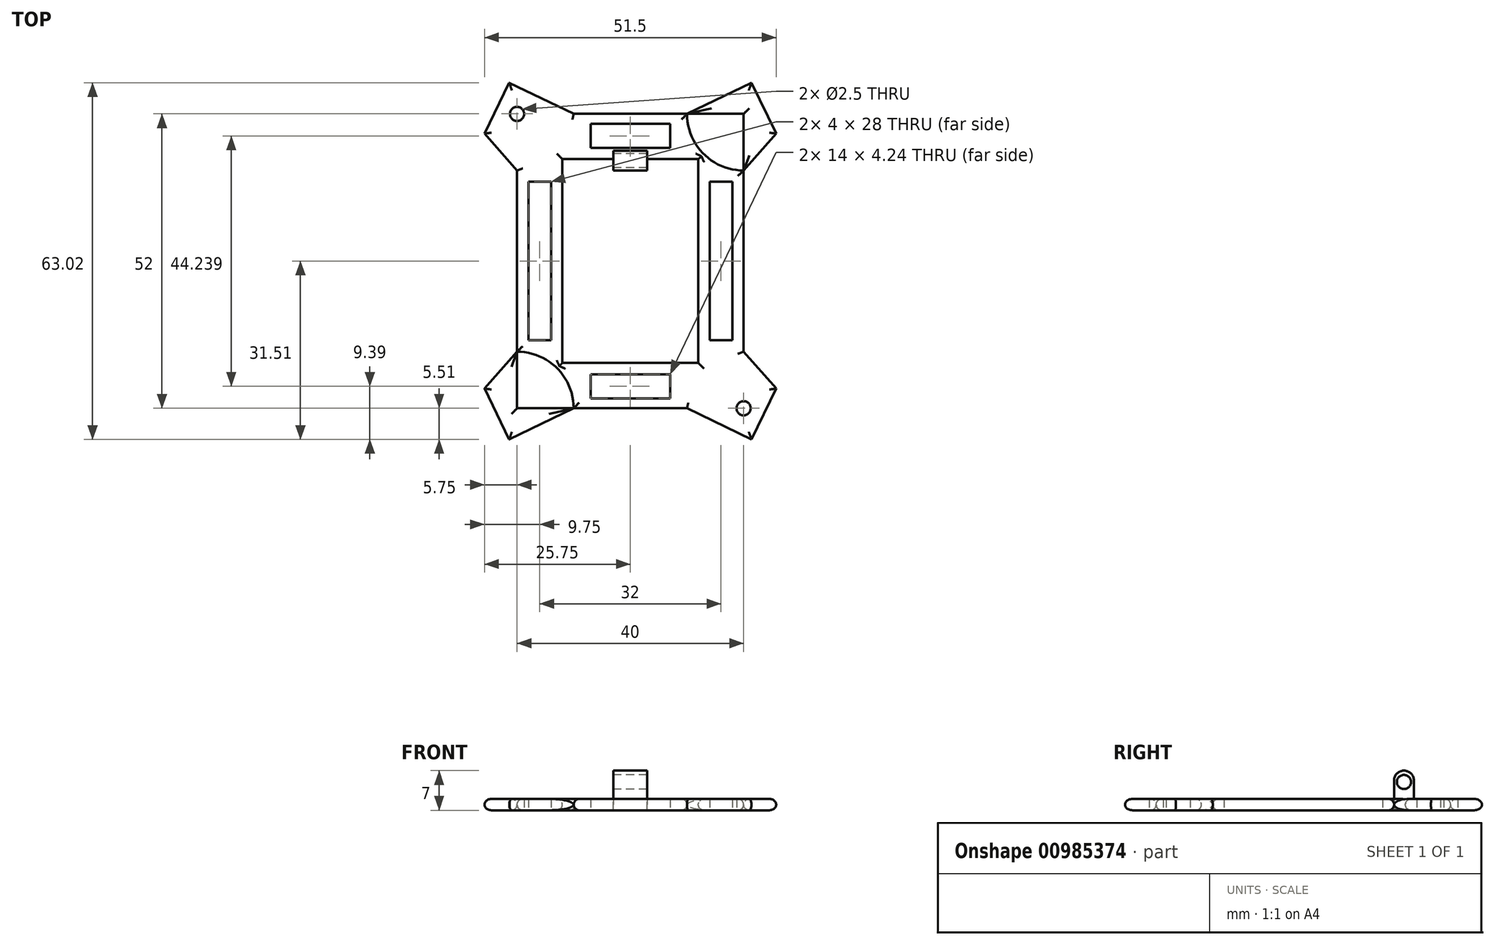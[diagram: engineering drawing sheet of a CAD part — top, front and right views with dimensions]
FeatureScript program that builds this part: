
annotation { "Feature Type Name" : "Feature", "Feature Type Description" : "" }
export const myFeature = defineFeature(function(context is Context, id is Id, definition is map)
    precondition{}
    {
        {
            var Q0;
            Q0=qCreatedBy(makeId("Top.planeOp"),FACE);
            var sketch = newSketch(context, id + "F0", { "sketchPlane" : qUnion([Q0])});
            skPoint(sketch, "E0.middle", {"position": v(0, 0) * mm});
            skLineSegment(sketch, "E1.bottom", {"start": v(10, -16) * mm, "end": v(-10, -16) * mm});
            skLineSegment(sketch, "E1.top", {"start": v(10, 16) * mm, "end": v(-10, 16) * mm});
            skLineSegment(sketch, "E1.left", {"start": v(10, -16) * mm, "end": v(10, 16) * mm});
            skLineSegment(sketch, "E1.right", {"start": v(-10, -16) * mm, "end": v(-10, 16) * mm});
            skLineSegment(sketch, "E2.bottom", {"start": v(12, 18) * mm, "end": v(-12, 18) * mm});
            skLineSegment(sketch, "E2.top", {"start": v(12, -18) * mm, "end": v(-12, -18) * mm});
            skLineSegment(sketch, "E2.left", {"start": v(12, 18) * mm, "end": v(12, -18) * mm});
            skLineSegment(sketch, "E2.right", {"start": v(-12, 18) * mm, "end": v(-12, -18) * mm});
            skLineSegment(sketch, "E3.bottom", {"start": v(20, -26) * mm, "end": v(-20, -26) * mm});
            skLineSegment(sketch, "E3.top", {"start": v(20, 26) * mm, "end": v(-20, 26) * mm});
            skLineSegment(sketch, "E3.left", {"start": v(20, -26) * mm, "end": v(20, 26) * mm});
            skLineSegment(sketch, "E3.right", {"start": v(-20, -26) * mm, "end": v(-20, 26) * mm});
            skCircle(sketch, "E4", {"center": v(-20, 26) * mm, "radius": 10 * mm});
            skCircle(sketch, "E5", {"center": v(20, 26) * mm, "radius": 10 * mm});
            skCircle(sketch, "E6", {"center": v(20, -26) * mm, "radius": 10 * mm});
            skCircle(sketch, "E7", {"center": v(-20, -26) * mm, "radius": 10 * mm});
            skCircle(sketch, "E8", {"center": v(-20, 26) * mm, "radius": 1.25 * mm});
            skCircle(sketch, "E9.MirrorC", {"center": v(20, 26) * mm, "radius": 1.25 * mm});
            skCircle(sketch, "E10.MirrorC", {"center": v(-20, -26) * mm, "radius": 1.25 * mm});
            skCircle(sketch, "E11.MirrorC", {"center": v(20, -26) * mm, "radius": 1.25 * mm});
            skLineSegment(sketch, "E12", {"start": v(-3, 16) * mm, "end": v(-3, 18) * mm});
            skLineSegment(sketch, "E13", {"start": v(3, 16) * mm, "end": v(3, 18) * mm});
            skLineSegment(sketch, "E14.bottom", {"start": v(-3, 18) * mm, "end": v(3, 18) * mm});
            skLineSegment(sketch, "E14.top", {"start": v(-3, 19.5) * mm, "end": v(3, 19.5) * mm});
            skLineSegment(sketch, "E14.left", {"start": v(-3, 18) * mm, "end": v(-3, 19.5) * mm});
            skLineSegment(sketch, "E14.right", {"start": v(3, 18) * mm, "end": v(3, 19.5) * mm});
            skLineSegment(sketch, "E15", {"start": v(-10, 26) * mm, "end": v(-26.2, 33.85) * mm});
            skLineSegment(sketch, "E16", {"start": v(-29.92, 27.25) * mm, "end": v(-20, 16) * mm});
            skLineSegment(sketch, "E17.MirrorCS", {"start": v(10, 26) * mm, "end": v(26.2, 33.85) * mm});
            skLineSegment(sketch, "E18.MirrorCS", {"start": v(29.92, 27.25) * mm, "end": v(20, 16) * mm});
            skLineSegment(sketch, "E19.MirrorCS", {"start": v(29.92, -27.25) * mm, "end": v(20, -16) * mm});
            skLineSegment(sketch, "E20.MirrorCS", {"start": v(10, -26) * mm, "end": v(26.2, -33.85) * mm});
            skLineSegment(sketch, "E21.MirrorCS", {"start": v(-10, -26) * mm, "end": v(-26.2, -33.85) * mm});
            skLineSegment(sketch, "E22.MirrorCS", {"start": v(-29.92, -27.25) * mm, "end": v(-20, -16) * mm});
            skLineSegment(sketch, "E23", {"start": v(-10, 16) * mm, "end": v(-10, 18) * mm});
            skLineSegment(sketch, "E24", {"start": v(10, 16) * mm, "end": v(10, 18) * mm});
            skLineSegment(sketch, "E25", {"start": v(-21.39, 31.51) * mm, "end": v(-25.75, 22.51) * mm});
            skLineSegment(sketch, "E26.MirrorCS", {"start": v(21.39, 31.51) * mm, "end": v(25.75, 22.51) * mm});
            skLineSegment(sketch, "E27.MirrorCS", {"start": v(-21.39, -31.51) * mm, "end": v(-25.75, -22.51) * mm});
            skLineSegment(sketch, "E28.MirrorCS", {"start": v(21.39, -31.51) * mm, "end": v(25.75, -22.51) * mm});
            skLineSegment(sketch, "E29.bottom", {"start": v(-18, 14) * mm, "end": v(-14, 14) * mm});
            skLineSegment(sketch, "E29.top", {"start": v(-18, -14) * mm, "end": v(-14, -14) * mm});
            skLineSegment(sketch, "E29.left", {"start": v(-18, 14) * mm, "end": v(-18, -14) * mm});
            skLineSegment(sketch, "E29.right", {"start": v(-14, 14) * mm, "end": v(-14, -14) * mm});
            skLineSegment(sketch, "E30.MirrorCS", {"start": v(14, 14) * mm, "end": v(14, -14) * mm});
            skLineSegment(sketch, "E31.MirrorCS", {"start": v(18, 14) * mm, "end": v(14, 14) * mm});
            skLineSegment(sketch, "E32.MirrorCS", {"start": v(18, 14) * mm, "end": v(18, -14) * mm});
            skLineSegment(sketch, "E33.MirrorCS", {"start": v(18, -14) * mm, "end": v(14, -14) * mm});
            skLineSegment(sketch, "E34.bottom", {"start": v(-7, -20) * mm, "end": v(7, -20) * mm});
            skLineSegment(sketch, "E34.top", {"start": v(-7, -24.24) * mm, "end": v(7, -24.24) * mm});
            skLineSegment(sketch, "E34.left", {"start": v(-7, -20) * mm, "end": v(-7, -24.24) * mm});
            skLineSegment(sketch, "E34.right", {"start": v(7, -20) * mm, "end": v(7, -24.24) * mm});
            skLineSegment(sketch, "E35.MirrorCS", {"start": v(-7, 20) * mm, "end": v(7, 20) * mm});
            skLineSegment(sketch, "E36.MirrorCS", {"start": v(-7, 20) * mm, "end": v(-7, 24.24) * mm});
            skLineSegment(sketch, "E37.MirrorCS", {"start": v(-7, 24.24) * mm, "end": v(7, 24.24) * mm});
            skLineSegment(sketch, "E38.MirrorCS", {"start": v(7, 20) * mm, "end": v(7, 24.24) * mm});
            skSolve(sketch);
        }
        {
            var Q0;
            {var subQ0=sQuery(id+"F0.wireOp",EDGE,"XfmaCdGe-Nsh5-LR8N-U050-nXJdRo87k7nu");Q0=makeQuery(id+"F0.imprint","IMPRINT",FACE,{"disambiguationData":[TD([[makeQuery(id+"F0.imprint","IMPRINT",EDGE,{"derivedFrom":subQ0}),-1.0]])]});}
            var Q1;
            {var subQ0=sQuery(id+"F0.wireOp",EDGE,"67c493aa-9df7-43f4-b791-e47cdcb916b60.MirrorCS");Q1=makeQuery(id+"F0.imprint","IMPRINT",FACE,{"disambiguationData":[TD([[makeQuery(id+"F0.imprint","IMPRINT",EDGE,{"derivedFrom":subQ0}),-1.0]])]});}
            var Q2;
            {var subQ0=sQuery(id+"F0.wireOp",EDGE,"3c266ea2-0ddf-4ded-b89f-077357a7d8e80.MirrorCS");Q2=makeQuery(id+"F0.imprint","IMPRINT",FACE,{"disambiguationData":[TD([[makeQuery(id+"F0.imprint","IMPRINT",EDGE,{"derivedFrom":subQ0}),-1.0]])]});}
            var Q3;
            {var subQ0=sQuery(id+"F0.wireOp",EDGE,"ab4d64e5-a29a-4c87-9f54-f3676ced8fba0.MirrorCS");Q3=makeQuery(id+"F0.imprint","IMPRINT",FACE,{"disambiguationData":[TD([[makeQuery(id+"F0.imprint","IMPRINT",EDGE,{"derivedFrom":subQ0}),1.0]])]});}
            var Q4;
            Q4=makeQuery(id+"F0.imprint","IMPRINT",FACE,{"disambiguationData":[TD([[makeQuery(id+"F0.imprint","IMPRINT",EDGE,{"derivedFrom":sQuery(id+"F0.wireOp",EDGE,"oP3ZfhLO-5z78-oQSo-uuvH-yzJxo6IJEnQO")}),-1.0]])]});
            var Q5;
            Q5=makeQuery(id+"F0.imprint","IMPRINT",FACE,{"disambiguationData":[TD([[makeQuery(id+"F0.imprint","IMPRINT",EDGE,{"derivedFrom":sQuery(id+"F0.wireOp",EDGE,"5d5cfb4f-1e90-434a-910e-95713f9e32be0.MirrorC")}),1.0]])]});
            var Q6;
            Q6=makeQuery(id+"F0.imprint","IMPRINT",FACE,{"disambiguationData":[TD([[makeQuery(id+"F0.imprint","IMPRINT",EDGE,{"derivedFrom":sQuery(id+"F0.wireOp",EDGE,"24c43ebd-9ed0-4dd5-8c82-3635907a6bdc0.MirrorC")}),-1.0]])]});
            var Q7;
            Q7=makeQuery(id+"F0.imprint","IMPRINT",FACE,{"disambiguationData":[TD([[makeQuery(id+"F0.imprint","IMPRINT",EDGE,{"derivedFrom":sQuery(id+"F0.wireOp",EDGE,"ed7e95fd-fa47-4424-be7c-35b6ced3335c0.MirrorC")}),1.0]])]});
            var Q8;
            Q8=makeQuery(id+"F0.imprint","IMPRINT",FACE,{"disambiguationData":[TD([[makeQuery(id+"F0.imprint","IMPRINT",EDGE,{"derivedFrom":sQuery(id+"F0.wireOp",EDGE,"E2.top")}),1.0]])]});
            var Q9;
            {var subQ1=sQuery(id+"F0.wireOp",EDGE,"E3.top");var subQ3=sQuery(id+"F0.wireOp",EDGE,"E8");var subQ4=makeQuery(id+"F0.imprint","INTERSECT",VERTEX,{"derivedFrom":[subQ1,subQ3]});Q9=makeQuery(id+"F0.imprint","IMPRINT",FACE,{"disambiguationData":[TD([[makeQuery(id+"F0.imprint","IMPRINT",EDGE,{"disambiguationData":[TD([[subQ4,1.0]])],"derivedFrom":subQ3}),-1.0]])]});}
            var Q10;
            {var subQ4=sQuery(id+"F0.wireOp",EDGE,"E25");Q10=makeQuery(id+"F0.imprint","IMPRINT",FACE,{"disambiguationData":[TD([[makeQuery(id+"F0.imprint","IMPRINT",EDGE,{"derivedFrom":subQ4}),1.0]])]});}
            var Q11;
            {var subQ1=sQuery(id+"F0.wireOp",EDGE,"E3.top");var subQ3=sQuery(id+"F0.wireOp",EDGE,"E9.MirrorC");var subQ4=makeQuery(id+"F0.imprint","INTERSECT",VERTEX,{"derivedFrom":[subQ1,subQ3]});Q11=makeQuery(id+"F0.imprint","IMPRINT",FACE,{"disambiguationData":[TD([[makeQuery(id+"F0.imprint","IMPRINT",EDGE,{"disambiguationData":[TD([[subQ4,1.0]])],"derivedFrom":subQ3}),1.0]])]});}
            var Q12;
            {var subQ4=sQuery(id+"F0.wireOp",EDGE,"E26.MirrorCS");Q12=makeQuery(id+"F0.imprint","IMPRINT",FACE,{"disambiguationData":[TD([[makeQuery(id+"F0.imprint","IMPRINT",EDGE,{"derivedFrom":subQ4}),-1.0]])]});}
            var Q13;
            {var subQ1=sQuery(id+"F0.wireOp",EDGE,"E3.bottom");var subQ3=sQuery(id+"F0.wireOp",EDGE,"E11.MirrorC");var subQ4=makeQuery(id+"F0.imprint","INTERSECT",VERTEX,{"derivedFrom":[subQ1,subQ3]});Q13=makeQuery(id+"F0.imprint","IMPRINT",FACE,{"disambiguationData":[TD([[makeQuery(id+"F0.imprint","IMPRINT",EDGE,{"disambiguationData":[TD([[subQ4,1.0]])],"derivedFrom":subQ3}),-1.0]])]});}
            var Q14;
            {var subQ8=sQuery(id+"F0.wireOp",EDGE,"E28.MirrorCS");Q14=makeQuery(id+"F0.imprint","IMPRINT",FACE,{"disambiguationData":[TD([[makeQuery(id+"F0.imprint","IMPRINT",EDGE,{"derivedFrom":subQ8}),1.0]])]});}
            var Q15;
            {var subQ8=sQuery(id+"F0.wireOp",EDGE,"E27.MirrorCS");Q15=makeQuery(id+"F0.imprint","IMPRINT",FACE,{"disambiguationData":[TD([[makeQuery(id+"F0.imprint","IMPRINT",EDGE,{"derivedFrom":subQ8}),-1.0]])]});}
            var Q16;
            {var subQ1=sQuery(id+"F0.wireOp",EDGE,"E3.bottom");var subQ3=sQuery(id+"F0.wireOp",EDGE,"E10.MirrorC");var subQ4=makeQuery(id+"F0.imprint","INTERSECT",VERTEX,{"derivedFrom":[subQ1,subQ3]});Q16=makeQuery(id+"F0.imprint","IMPRINT",FACE,{"disambiguationData":[TD([[makeQuery(id+"F0.imprint","IMPRINT",EDGE,{"disambiguationData":[TD([[subQ4,1.0]])],"derivedFrom":subQ3}),1.0]])]});}
            extrude(context, id + "F1", {"entities" : qUnion([Q0, Q1, Q2, Q3, Q4, Q5, Q6, Q7, Q8, Q9, Q10, Q11, Q12, Q13, Q14, Q15, Q16]), "depth" : 2 * mm, "offsetDistance" : 25 * mm});
        }
        {
            var Q0;
            {var subQ0=sQuery(id+"F0.wireOp",EDGE,"E12");Q0=makeQuery(id+"F0.imprint","IMPRINT",FACE,{"disambiguationData":[TD([[makeQuery(id+"F0.imprint","IMPRINT",EDGE,{"derivedFrom":subQ0}),-1.0]])]});}
            var Q1;
            Q1=makeQuery(id+"F0.imprint","IMPRINT",FACE,{"disambiguationData":[TD([[makeQuery(id+"F0.imprint","IMPRINT",EDGE,{"derivedFrom":sQuery(id+"F0.wireOp",EDGE,"E14.top")}),-1.0]])]});
            extrude(context, id + "F2", {"entities" : qUnion([Q0, Q1]), "operationType" : NewBodyOperationType.ADD, "depth" : 7 * mm, "offsetDistance" : 25 * mm});
        }
        {
            var Q0;
            Q0=makeQuery(id+"F2.opExtrude","CAP_EDGE",EDGE,{"disambiguationData":[OSD([sQuery(id+"F0.wireOp",EDGE,"E1.top")])],"isStart":false});
            var Q1;
            Q1=makeQuery(id+"F2.opExtrude","CAP_EDGE",EDGE,{"disambiguationData":[OSD([sQuery(id+"F0.wireOp",EDGE,"E2.bottom")])],"isStart":false});
            var Q2;
            Q2=makeQuery(id+"F2.opExtrude","CAP_EDGE",EDGE,{"disambiguationData":[OSD([sQuery(id+"F0.wireOp",EDGE,"E14.top")])],"isStart":false});
            fillet(context, id + "F3", {"entities" : qUnion([Q0, Q1, Q2]), "radius" : 1.75 * mm, "tangentPropagation" : true, "allowEdgeOverflow" : false});
        }
        {
            var Q0;
            Q0=makeQuery(id+"F2.opExtrude","SWEPT_FACE",FACE,{"disambiguationData":[OSD([sQuery(id+"F0.wireOp",EDGE,"E12"),sQuery(id+"F0.wireOp",EDGE,"E14.left")])]});
            var sketch = newSketch(context, id + "F4", { "sketchPlane" : qUnion([Q0])});
            skCircle(sketch, "E39", {"center": v(-17.75, 5) * mm, "radius": 1.25 * mm});
            skPoint(sketch, "E39.centerSnap0", {"position": v(-17.75, 7) * mm});
            skSolve(sketch);
        }
        {
            var Q0;
            Q0=makeQuery(id+"F4.imprint","IMPRINT",FACE,{"disambiguationData":[TD([[makeQuery(id+"F4.imprint","IMPRINT",EDGE,{"derivedFrom":sQuery(id+"F4.wireOp",EDGE,"E39")}),1.0]])]});
            extrude(context, id + "F5", {"entities" : qUnion([Q0]), "operationType" : NewBodyOperationType.REMOVE, "oppositeDirection" : true, "depth" : 25 * mm, "offsetDistance" : 25 * mm});
        }
        {
            var Q0;
            Q0=makeQuery(id+"F1.opExtrude","CAP_EDGE",EDGE,{"disambiguationData":[OSD([sQuery(id+"F0.wireOp",EDGE,"E3.right")])],"isStart":false});
            var Q1;
            Q1=makeQuery(id+"F1.opExtrude","CAP_EDGE",EDGE,{"disambiguationData":[OSD([sQuery(id+"F0.wireOp",EDGE,"E7")])],"isStart":false});
            var Q2;
            Q2=makeQuery(id+"F1.opExtrude","CAP_EDGE",EDGE,{"disambiguationData":[OSD([sQuery(id+"F0.wireOp",EDGE,"E3.bottom")])],"isStart":false});
            var Q3;
            Q3=makeQuery(id+"F1.opExtrude","CAP_EDGE",EDGE,{"disambiguationData":[OSD([sQuery(id+"F0.wireOp",EDGE,"E6")])],"isStart":false});
            var Q4;
            Q4=makeQuery(id+"F1.opExtrude","CAP_EDGE",EDGE,{"disambiguationData":[OSD([sQuery(id+"F0.wireOp",EDGE,"E3.left")])],"isStart":false});
            var Q5;
            Q5=makeQuery(id+"F1.opExtrude","CAP_EDGE",EDGE,{"disambiguationData":[OSD([sQuery(id+"F0.wireOp",EDGE,"E5")])],"isStart":false});
            var Q6;
            Q6=makeQuery(id+"F1.opExtrude","CAP_EDGE",EDGE,{"disambiguationData":[OSD([sQuery(id+"F0.wireOp",EDGE,"E3.top")])],"isStart":false});
            var Q7;
            Q7=makeQuery(id+"F1.opExtrude","CAP_EDGE",EDGE,{"disambiguationData":[OSD([sQuery(id+"F0.wireOp",EDGE,"E4")])],"isStart":false});
            var Q8;
            Q8=makeQuery(id+"F1.opExtrude","CAP_EDGE",EDGE,{"disambiguationData":[OSD([sQuery(id+"F0.wireOp",EDGE,"E4")])],"isStart":true});
            var Q9;
            Q9=makeQuery(id+"F1.opExtrude","CAP_EDGE",EDGE,{"disambiguationData":[OSD([sQuery(id+"F0.wireOp",EDGE,"E3.top")])],"isStart":true});
            var Q10;
            Q10=makeQuery(id+"F1.opExtrude","CAP_EDGE",EDGE,{"disambiguationData":[OSD([sQuery(id+"F0.wireOp",EDGE,"E5")])],"isStart":true});
            var Q11;
            Q11=makeQuery(id+"F1.opExtrude","CAP_EDGE",EDGE,{"disambiguationData":[OSD([sQuery(id+"F0.wireOp",EDGE,"E3.left")])],"isStart":true});
            var Q12;
            Q12=makeQuery(id+"F1.opExtrude","CAP_EDGE",EDGE,{"disambiguationData":[OSD([sQuery(id+"F0.wireOp",EDGE,"E7")])],"isStart":true});
            var Q13;
            Q13=makeQuery(id+"F1.opExtrude","CAP_EDGE",EDGE,{"disambiguationData":[OSD([sQuery(id+"F0.wireOp",EDGE,"E3.bottom")])],"isStart":true});
            var Q14;
            Q14=makeQuery(id+"F1.opExtrude","CAP_EDGE",EDGE,{"disambiguationData":[OSD([sQuery(id+"F0.wireOp",EDGE,"E6")])],"isStart":true});
            var Q15;
            Q15=makeQuery(id+"F1.opExtrude","CAP_EDGE",EDGE,{"disambiguationData":[OSD([sQuery(id+"F0.wireOp",EDGE,"E3.right")])],"isStart":true});
            var Q16;
            Q16=makeQuery(id+"F1.opExtrude","CAP_EDGE",EDGE,{"disambiguationData":[OSD([sQuery(id+"F0.wireOp",EDGE,"E1.right")])],"isStart":false});
            var Q17;
            {var subQ0=sQuery(id+"F0.wireOp",EDGE,"E1.top");Q17=makeQuery(id+"F1.opExtrude","CAP_EDGE",EDGE,{"disambiguationData":[OSD([subQ0]),TDD([makeQuery(id+"F0.imprint","IMPRINT",EDGE,{"disambiguationData":[TD([[makeQuery(id+"F0.imprint","INTERSECT",VERTEX,{"derivedFrom":[subQ0,sQuery(id+"F0.wireOp",EDGE,"E1.right")]}),1.0]])],"derivedFrom":subQ0})])],"isStart":false});}
            var Q18;
            {var subQ0=sQuery(id+"F0.wireOp",EDGE,"E1.top");Q18=makeQuery(id+"F1.opExtrude","CAP_EDGE",EDGE,{"disambiguationData":[OSD([subQ0]),TDD([makeQuery(id+"F0.imprint","IMPRINT",EDGE,{"disambiguationData":[TD([[makeQuery(id+"F0.imprint","INTERSECT",VERTEX,{"derivedFrom":[subQ0,sQuery(id+"F0.wireOp",EDGE,"E1.left")]}),-1.0]])],"derivedFrom":subQ0})])],"isStart":false});}
            var Q19;
            Q19=makeQuery(id+"F1.opExtrude","CAP_EDGE",EDGE,{"disambiguationData":[OSD([sQuery(id+"F0.wireOp",EDGE,"E1.left")])],"isStart":false});
            var Q20;
            Q20=makeQuery(id+"F1.opExtrude","CAP_EDGE",EDGE,{"disambiguationData":[OSD([sQuery(id+"F0.wireOp",EDGE,"E1.bottom")])],"isStart":false});
            var Q21;
            Q21=makeQuery(id+"F2.opExtrude","CAP_EDGE",EDGE,{"disambiguationData":[OSD([sQuery(id+"F0.wireOp",EDGE,"E1.top")])],"isStart":true});
            var Q22;
            Q22=makeQuery(id+"F1.opExtrude","CAP_EDGE",EDGE,{"disambiguationData":[OSD([sQuery(id+"F0.wireOp",EDGE,"E1.right")])],"isStart":true});
            var Q23;
            Q23=makeQuery(id+"F1.opExtrude","CAP_EDGE",EDGE,{"disambiguationData":[OSD([sQuery(id+"F0.wireOp",EDGE,"E1.bottom")])],"isStart":true});
            var Q24;
            Q24=makeQuery(id+"F1.opExtrude","CAP_EDGE",EDGE,{"disambiguationData":[OSD([sQuery(id+"F0.wireOp",EDGE,"E1.left")])],"isStart":true});
            var Q25;
            Q25=makeQuery(id+"F1.opExtrude","CAP_EDGE",EDGE,{"disambiguationData":[OSD([sQuery(id+"F0.wireOp",EDGE,"E16")])],"isStart":false});
            var Q26;
            Q26=makeQuery(id+"F1.opExtrude","CAP_EDGE",EDGE,{"disambiguationData":[OSD([sQuery(id+"F0.wireOp",EDGE,"E16")])],"isStart":true});
            var Q27;
            Q27=makeQuery(id+"F1.opExtrude","CAP_EDGE",EDGE,{"disambiguationData":[OSD([sQuery(id+"F0.wireOp",EDGE,"E15")])],"isStart":false});
            var Q28;
            Q28=makeQuery(id+"F1.opExtrude","CAP_EDGE",EDGE,{"disambiguationData":[OSD([sQuery(id+"F0.wireOp",EDGE,"E15")])],"isStart":true});
            var Q29;
            Q29=makeQuery(id+"F1.opExtrude","CAP_EDGE",EDGE,{"disambiguationData":[OSD([sQuery(id+"F0.wireOp",EDGE,"E17.MirrorCS")])],"isStart":false});
            var Q30;
            Q30=makeQuery(id+"F1.opExtrude","CAP_EDGE",EDGE,{"disambiguationData":[OSD([sQuery(id+"F0.wireOp",EDGE,"E17.MirrorCS")])],"isStart":true});
            var Q31;
            Q31=makeQuery(id+"F1.opExtrude","CAP_EDGE",EDGE,{"disambiguationData":[OSD([sQuery(id+"F0.wireOp",EDGE,"E18.MirrorCS")])],"isStart":false});
            var Q32;
            Q32=makeQuery(id+"F1.opExtrude","CAP_EDGE",EDGE,{"disambiguationData":[OSD([sQuery(id+"F0.wireOp",EDGE,"E18.MirrorCS")])],"isStart":true});
            var Q33;
            Q33=makeQuery(id+"F1.opExtrude","CAP_EDGE",EDGE,{"disambiguationData":[OSD([sQuery(id+"F0.wireOp",EDGE,"E19.MirrorCS")])],"isStart":false});
            var Q34;
            Q34=makeQuery(id+"F1.opExtrude","CAP_EDGE",EDGE,{"disambiguationData":[OSD([sQuery(id+"F0.wireOp",EDGE,"E19.MirrorCS")])],"isStart":true});
            var Q35;
            Q35=makeQuery(id+"F1.opExtrude","CAP_EDGE",EDGE,{"disambiguationData":[OSD([sQuery(id+"F0.wireOp",EDGE,"E20.MirrorCS")])],"isStart":true});
            var Q36;
            Q36=makeQuery(id+"F1.opExtrude","CAP_EDGE",EDGE,{"disambiguationData":[OSD([sQuery(id+"F0.wireOp",EDGE,"E20.MirrorCS")])],"isStart":false});
            var Q37;
            Q37=makeQuery(id+"F1.opExtrude","CAP_EDGE",EDGE,{"disambiguationData":[OSD([sQuery(id+"F0.wireOp",EDGE,"E21.MirrorCS")])],"isStart":true});
            var Q38;
            Q38=makeQuery(id+"F1.opExtrude","CAP_EDGE",EDGE,{"disambiguationData":[OSD([sQuery(id+"F0.wireOp",EDGE,"E21.MirrorCS")])],"isStart":false});
            var Q39;
            Q39=makeQuery(id+"F1.opExtrude","CAP_EDGE",EDGE,{"disambiguationData":[OSD([sQuery(id+"F0.wireOp",EDGE,"E22.MirrorCS")])],"isStart":true});
            var Q40;
            Q40=makeQuery(id+"F1.opExtrude","CAP_EDGE",EDGE,{"disambiguationData":[OSD([sQuery(id+"F0.wireOp",EDGE,"E22.MirrorCS")])],"isStart":false});
            var Q41;
            {var subQ0=sQuery(id+"F0.wireOp",EDGE,"E2.bottom");var subQ1=makeQuery(id+"F0.imprint","INTERSECT",VERTEX,{"derivedFrom":[subQ0,sQuery(id+"F0.wireOp",EDGE,"E23")]});Q41=makeQuery(id+"F1.opExtrude","CAP_EDGE",EDGE,{"disambiguationData":[OSD([subQ0]),TDD([makeQuery(id+"F0.imprint","IMPRINT",EDGE,{"disambiguationData":[TD([[subQ1,1.0]])],"derivedFrom":subQ0}),makeQuery(id+"F0.imprint","IMPRINT",EDGE,{"disambiguationData":[TD([[makeQuery(id+"F0.imprint","INTERSECT",VERTEX,{"derivedFrom":[subQ0,sQuery(id+"F0.wireOp",EDGE,"E2.right")]}),1.0]])],"derivedFrom":subQ0})])],"isStart":false});}
            var Q42;
            Q42=makeQuery(id+"F1.opExtrude","CAP_EDGE",EDGE,{"disambiguationData":[OSD([sQuery(id+"F0.wireOp",EDGE,"E2.right")])],"isStart":false});
            var Q43;
            {var subQ0=sQuery(id+"F0.wireOp",EDGE,"E2.bottom");var subQ1=makeQuery(id+"F0.imprint","INTERSECT",VERTEX,{"derivedFrom":[subQ0,sQuery(id+"F0.wireOp",EDGE,"E24")]});Q43=makeQuery(id+"F1.opExtrude","CAP_EDGE",EDGE,{"disambiguationData":[OSD([subQ0]),TDD([makeQuery(id+"F0.imprint","IMPRINT",EDGE,{"disambiguationData":[TD([[subQ1,-1.0]])],"derivedFrom":subQ0}),makeQuery(id+"F0.imprint","IMPRINT",EDGE,{"disambiguationData":[TD([[subQ1,1.0]])],"derivedFrom":subQ0})])],"isStart":false});}
            var Q44;
            Q44=makeQuery(id+"F1.opExtrude","CAP_EDGE",EDGE,{"disambiguationData":[OSD([sQuery(id+"F0.wireOp",EDGE,"E2.left")])],"isStart":false});
            var Q45;
            Q45=makeQuery(id+"F1.opExtrude","CAP_EDGE",EDGE,{"disambiguationData":[OSD([sQuery(id+"F0.wireOp",EDGE,"E2.left")])],"isStart":true});
            var Q46;
            Q46=makeQuery(id+"F1.opExtrude","CAP_EDGE",EDGE,{"disambiguationData":[OSD([sQuery(id+"F0.wireOp",EDGE,"E2.right")])],"isStart":true});
            var Q47;
            {var subQ0=sQuery(id+"F0.wireOp",EDGE,"E2.bottom");var subQ1=makeQuery(id+"F0.imprint","INTERSECT",VERTEX,{"derivedFrom":[subQ0,sQuery(id+"F0.wireOp",EDGE,"E24")]});Q47=makeQuery(id+"F1.opExtrude","CAP_EDGE",EDGE,{"disambiguationData":[OSD([subQ0]),TDD([makeQuery(id+"F0.imprint","IMPRINT",EDGE,{"disambiguationData":[TD([[subQ1,-1.0]])],"derivedFrom":subQ0}),makeQuery(id+"F0.imprint","IMPRINT",EDGE,{"disambiguationData":[TD([[subQ1,1.0]])],"derivedFrom":subQ0})])],"isStart":true});}
            var Q48;
            {var subQ0=sQuery(id+"F0.wireOp",EDGE,"E2.bottom");var subQ1=makeQuery(id+"F0.imprint","INTERSECT",VERTEX,{"derivedFrom":[subQ0,sQuery(id+"F0.wireOp",EDGE,"E23")]});Q48=makeQuery(id+"F1.opExtrude","CAP_EDGE",EDGE,{"disambiguationData":[OSD([subQ0]),TDD([makeQuery(id+"F0.imprint","IMPRINT",EDGE,{"disambiguationData":[TD([[subQ1,1.0]])],"derivedFrom":subQ0}),makeQuery(id+"F0.imprint","IMPRINT",EDGE,{"disambiguationData":[TD([[makeQuery(id+"F0.imprint","INTERSECT",VERTEX,{"derivedFrom":[subQ0,sQuery(id+"F0.wireOp",EDGE,"E2.right")]}),1.0]])],"derivedFrom":subQ0})])],"isStart":true});}
            var Q49;
            Q49=makeQuery(id+"F1.opExtrude","CAP_EDGE",EDGE,{"disambiguationData":[OSD([sQuery(id+"F0.wireOp",EDGE,"E2.top")])],"isStart":false});
            var Q50;
            Q50=makeQuery(id+"F1.opExtrude","CAP_EDGE",EDGE,{"disambiguationData":[OSD([sQuery(id+"F0.wireOp",EDGE,"E2.top")])],"isStart":true});
            var Q51;
            Q51=makeQuery(id+"F1.opExtrude","CAP_EDGE",EDGE,{"disambiguationData":[OSD([sQuery(id+"F0.wireOp",EDGE,"E27.MirrorCS")])],"isStart":false});
            var Q52;
            Q52=makeQuery(id+"F1.opExtrude","CAP_EDGE",EDGE,{"disambiguationData":[OSD([sQuery(id+"F0.wireOp",EDGE,"E27.MirrorCS")])],"isStart":true});
            var Q53;
            Q53=makeQuery(id+"F1.opExtrude","CAP_EDGE",EDGE,{"disambiguationData":[OSD([sQuery(id+"F0.wireOp",EDGE,"E28.MirrorCS")])],"isStart":false});
            var Q54;
            Q54=makeQuery(id+"F1.opExtrude","CAP_EDGE",EDGE,{"disambiguationData":[OSD([sQuery(id+"F0.wireOp",EDGE,"E28.MirrorCS")])],"isStart":true});
            var Q55;
            Q55=makeQuery(id+"F1.opExtrude","CAP_EDGE",EDGE,{"disambiguationData":[OSD([sQuery(id+"F0.wireOp",EDGE,"E26.MirrorCS")])],"isStart":false});
            var Q56;
            Q56=makeQuery(id+"F1.opExtrude","CAP_EDGE",EDGE,{"disambiguationData":[OSD([sQuery(id+"F0.wireOp",EDGE,"E26.MirrorCS")])],"isStart":true});
            var Q57;
            Q57=makeQuery(id+"F1.opExtrude","CAP_EDGE",EDGE,{"disambiguationData":[OSD([sQuery(id+"F0.wireOp",EDGE,"E25")])],"isStart":false});
            var Q58;
            Q58=makeQuery(id+"F1.opExtrude","CAP_EDGE",EDGE,{"disambiguationData":[OSD([sQuery(id+"F0.wireOp",EDGE,"E25")])],"isStart":true});
            fillet(context, id + "F6", {"entities" : qUnion([Q0, Q1, Q2, Q3, Q4, Q5, Q6, Q7, Q8, Q9, Q10, Q11, Q12, Q13, Q14, Q15, Q16, Q17, Q18, Q19, Q20, Q21, Q22, Q23, Q24, Q25, Q26, Q27, Q28, Q29, Q30, Q31, Q32, Q33, Q34, Q35, Q36, Q37, Q38, Q39, Q40, Q41, Q42, Q43, Q44, Q45, Q46, Q47, Q48, Q49, Q50, Q51, Q52, Q53, Q54, Q55, Q56, Q57, Q58]), "radius" : 1 * mm, "tangentPropagation" : true, "allowEdgeOverflow" : false});
        }
    });
